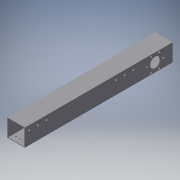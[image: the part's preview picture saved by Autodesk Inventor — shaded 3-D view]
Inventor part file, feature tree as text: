
AUTODESK INVENTOR PART (.ipt)
format: ipt  version: 2018 (Build 220112000, 112)  size: 187,904 bytes
history: native  units: in
note: dims shown in document units (in); Inventor stores cm internally (conversion verified against a paired STEP export)
features: extrude x5, sketch x5
ambient origin geometry x8: Origin, YZ Plane, XZ Plane, XY Plane, X Axis, Y Axis, Z Axis, Center Point
bodies: Solid1 (feature_tree)
feature tree (10):
  extrude  "Extrusion1"  Depth=2.0in
  extrude  "Extrusion2"  Depth=0.065in
  extrude  "Extrusion4"  Depth=0.065in
  extrude  "Extrusion5"  Depth=17.0in
  extrude  "Extrusion6"  Depth=2.0in
  sketch  "Sketch1"  dims[d0=2.0in d1=2.0in]
  sketch  "Sketch2"  dims[d2=0.065in d3=0.065in]
  sketch  "Sketch5"  dims[d4=0.065in d5=0.065in]
  sketch  "Sketch6"  dims[d6=17.0in d7=0.0in d8=4.5in]
  sketch  "Sketch7"  dims[d9=1.0in d10=1.0in d11=1.0in d12=1.0in d13=0.5in d14=0.2031in d15=0.2031in d16=0.2031in d19=0.2031in d20=0.2031in d21=0.2031in d22=0.5in d23=0.5in d24=0.5in d25=0.5in d26=0.5in d27=0.5in d28=11.0in d29=0.0in d36=2.0in d37=0.9375in d38=0.75in d39=0.2031in d40=1.0in d41=1.0in d42=2.3622in d44=360.0deg d46=2.0in d47=0.0in d48=1.0in d49=0.9375in d50=1.15in d51=2.0in d52=0.0in d53=0.2031in d54=1.0in d56=0.5in d57=0.2031in d58=0.2031in d59=0.5in d60=1.0in d61=0.5in d62=0.5in d63=1.0in d64=0.0in]
